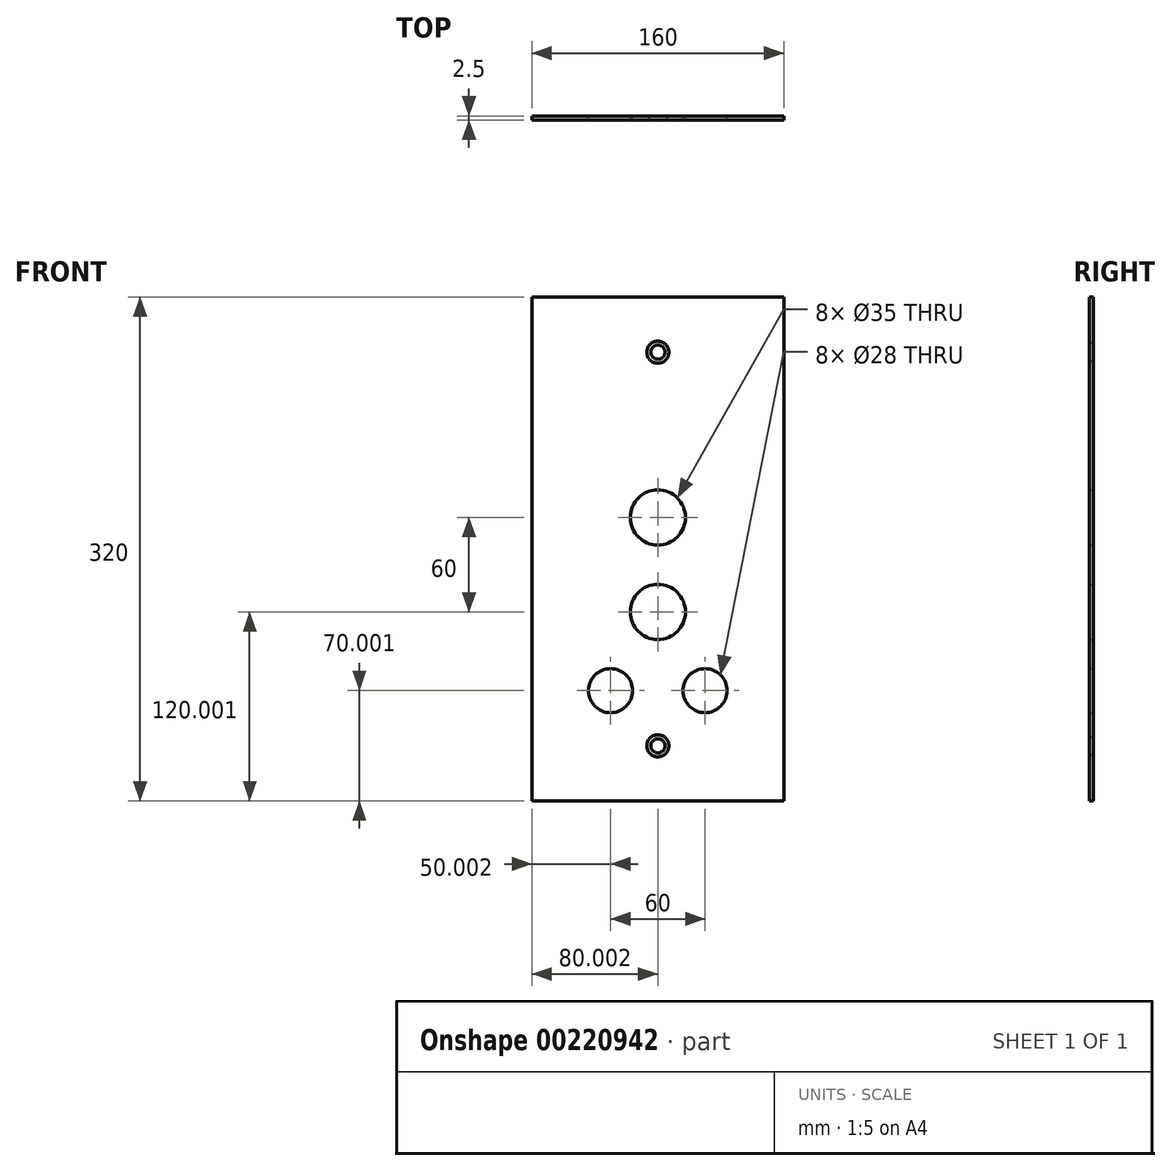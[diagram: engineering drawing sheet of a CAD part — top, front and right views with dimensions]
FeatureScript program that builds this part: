
annotation { "Feature Type Name" : "Feature", "Feature Type Description" : "" }
export const myFeature = defineFeature(function(context is Context, id is Id, definition is map)
    precondition{}
    {
        {
            var Q0;
            Q0=qCreatedBy(makeId("Front.planeOp"),FACE);
            var sketch = newSketch(context, id + "F0", { "sketchPlane" : qUnion([Q0])});
            skLineSegment(sketch, "E0.bottom", {"start": v(-81.89, 189.68) * mm, "end": v(78.11, 189.68) * mm});
            skLineSegment(sketch, "E0.top", {"start": v(-81.89, -130.32) * mm, "end": v(78.11, -130.32) * mm});
            skLineSegment(sketch, "E0.left", {"start": v(-81.89, 189.68) * mm, "end": v(-81.89, -130.32) * mm});
            skLineSegment(sketch, "E0.right", {"start": v(78.11, 189.68) * mm, "end": v(78.11, -130.32) * mm});
            skLineSegment(sketch, "E1", {"start": v(-1.89, 189.68) * mm, "end": v(-1.89, -130.32) * mm, "construction": true});
            skCircle(sketch, "E2", {"center": v(-1.89, 154.68) * mm, "radius": 3 * mm});
            skCircle(sketch, "E3", {"center": v(-1.89, -95.32) * mm, "radius": 3 * mm});
            skCircle(sketch, "E4", {"center": v(-1.89, -10.32) * mm, "radius": 17.5 * mm});
            skCircle(sketch, "E5", {"center": v(-1.89, 49.68) * mm, "radius": 17.5 * mm});
            skLineSegment(sketch, "E6", {"start": v(-81.89, -60.32) * mm, "end": v(78.11, -60.32) * mm, "construction": true});
            skCircle(sketch, "E7", {"center": v(-31.89, -60.32) * mm, "radius": 14 * mm});
            skCircle(sketch, "E8", {"center": v(28.11, -60.32) * mm, "radius": 14 * mm});
            skSolve(sketch);
        }
        {
            var Q0;
            Q0=makeQuery(id+"F0.imprint","IMPRINT",FACE,{"disambiguationData":[TD([[makeQuery(id+"F0.imprint","IMPRINT",EDGE,{"derivedFrom":sQuery(id+"F0.wireOp",EDGE,"E0.bottom")}),-1.0]])]});
            extrude(context, id + "F1", {"entities" : qUnion([Q0]), "depth" : 2.5 * mm});
        }
        {
            var Q0;
            Q0=makeQuery(id+"F1.opExtrude","CAP_EDGE",EDGE,{"disambiguationData":[OSD([sQuery(id+"F0.wireOp",EDGE,"E2")])],"isStart":false});
            var Q1;
            Q1=makeQuery(id+"F1.opExtrude","CAP_EDGE",EDGE,{"disambiguationData":[OSD([sQuery(id+"F0.wireOp",EDGE,"E3")])],"isStart":false});
            chamfer(context, id + "F2", {"entities" : qUnion([Q0, Q1]), "chamferType" : ChamferType.OFFSET_ANGLE, "width" : 4 * mm, "oppositeDirection" : false, "angle" : 45 * degree, "tangentPropagation" : true});
        }
    });
